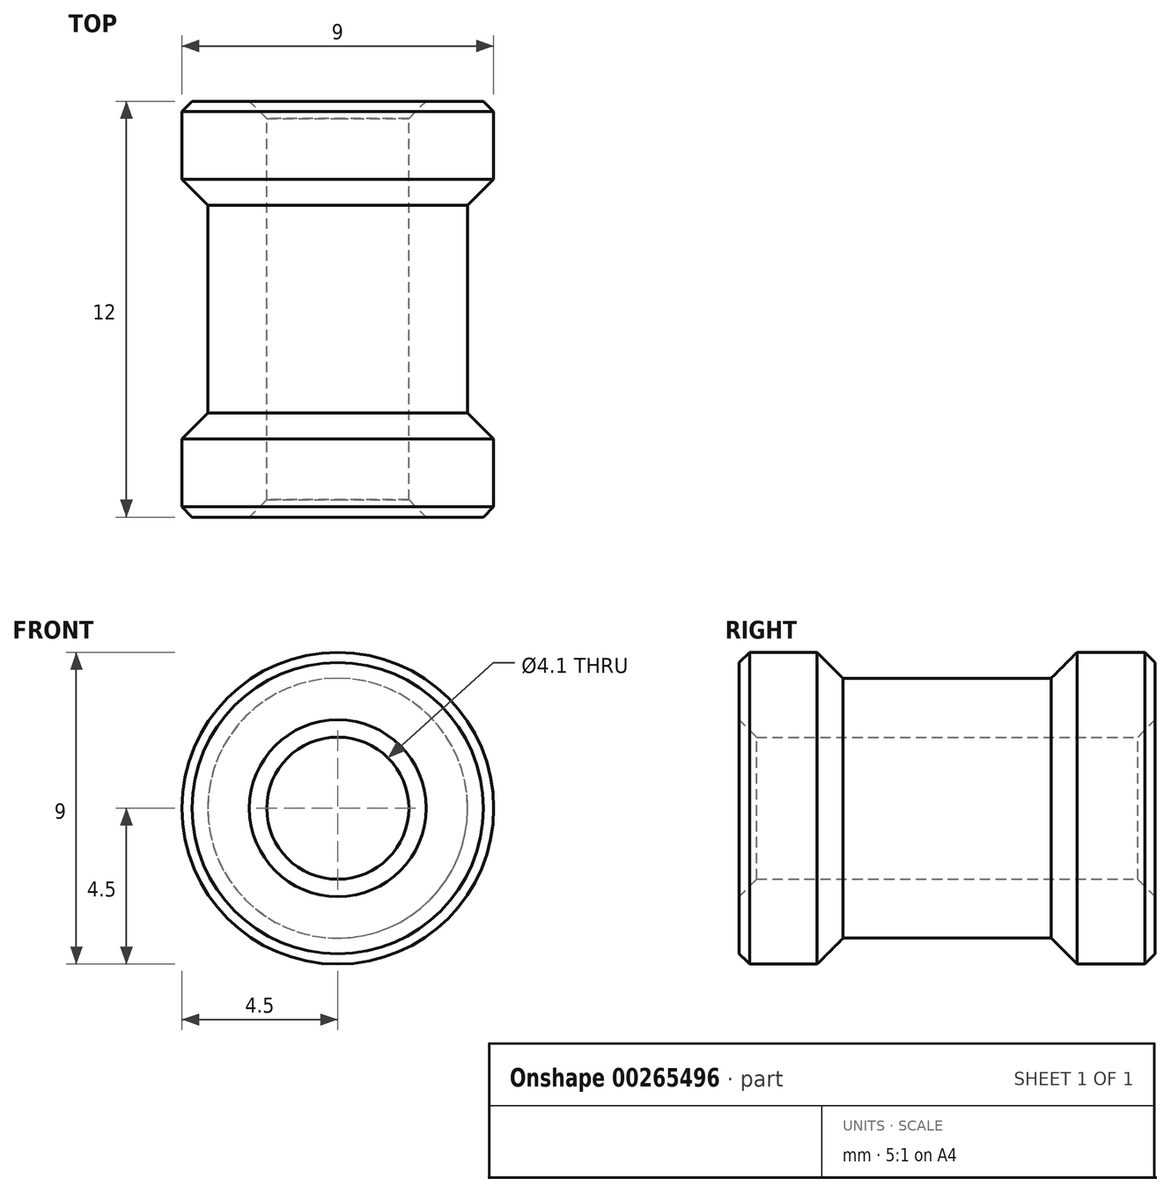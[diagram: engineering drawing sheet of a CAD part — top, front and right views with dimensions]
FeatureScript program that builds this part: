
annotation { "Feature Type Name" : "Feature", "Feature Type Description" : "" }
export const myFeature = defineFeature(function(context is Context, id is Id, definition is map)
    precondition{}
    {
        {
            var Q0;
            Q0=qCreatedBy(makeId("Front.planeOp"),FACE);
            var sketch = newSketch(context, id + "F0", { "sketchPlane" : qUnion([Q0])});
            skCircle(sketch, "E0", {"center": v(0, 0) * mm, "radius": 4.5 * mm});
            skCircle(sketch, "E1", {"center": v(0, 0) * mm, "radius": 2.05 * mm});
            skSolve(sketch);
        }
        {
            var Q0;
            Q0=makeQuery(id+"F0.imprint","IMPRINT",FACE,{"disambiguationData":[TD([[makeQuery(id+"F0.imprint","IMPRINT",EDGE,{"derivedFrom":sQuery(id+"F0.wireOp",EDGE,"E0")}),1.0]])]});
            extrude(context, id + "F1", {"entities" : qUnion([Q0]), "depth" : 12 * mm});
        }
        {
            var Q0;
            Q0=makeQuery(id+"F1.opExtrude","CAP_EDGE",EDGE,{"disambiguationData":[OSD([sQuery(id+"F0.wireOp",EDGE,"E0")])],"isStart":false});
            chamfer(context, id + "F2", {"entities" : qUnion([Q0]), "width" : 0.3 * mm, "tangentPropagation" : true});
        }
        {
            var Q0;
            Q0=makeQuery(id+"F1.opExtrude","CAP_EDGE",EDGE,{"disambiguationData":[OSD([sQuery(id+"F0.wireOp",EDGE,"E1")])],"isStart":false});
            chamfer(context, id + "F3", {"entities" : qUnion([Q0]), "width" : 0.5 * mm, "tangentPropagation" : true});
        }
        {
            var Q0;
            Q0=makeQuery(id+"F1.opExtrude","CAP_EDGE",EDGE,{"disambiguationData":[OSD([sQuery(id+"F0.wireOp",EDGE,"E1")])],"isStart":true});
            chamfer(context, id + "F4", {"entities" : qUnion([Q0]), "width" : 0.5 * mm, "tangentPropagation" : true});
        }
        {
            var Q0;
            Q0=makeQuery(id+"F1.opExtrude","CAP_EDGE",EDGE,{"disambiguationData":[OSD([sQuery(id+"F0.wireOp",EDGE,"E0")])],"isStart":true});
            chamfer(context, id + "F5", {"entities" : qUnion([Q0]), "width" : 0.3 * mm, "tangentPropagation" : true});
        }
        {
            var Q0;
            Q0=qCreatedBy(makeId("Top.planeOp"),FACE);
            var sketch = newSketch(context, id + "F6", { "sketchPlane" : qUnion([Q0])});
            skPoint(sketch, "E2.middle", {"position": v(0, 0) * mm});
            skLineSegment(sketch, "E3", {"start": v(0, 0) * mm, "end": v(0, -2) * mm});
            skLineSegment(sketch, "E4", {"start": v(-3.75, -2) * mm, "end": v(-3.75, -10) * mm});
            skLineSegment(sketch, "E5", {"start": v(-3.75, -10) * mm, "end": v(0, -10) * mm});
            skLineSegment(sketch, "E6", {"start": v(0, -2) * mm, "end": v(-3.75, -2) * mm});
            skLineSegment(sketch, "E7", {"start": v(0, -10) * mm, "end": v(0, -12) * mm});
            skLineSegment(sketch, "E8.bottom", {"start": v(-3.75, -2) * mm, "end": v(-4.53, -2) * mm});
            skLineSegment(sketch, "E8.top", {"start": v(-3.75, -10) * mm, "end": v(-4.53, -10) * mm});
            skLineSegment(sketch, "E8.right", {"start": v(-4.53, -2) * mm, "end": v(-4.53, -10) * mm});
            skLineSegment(sketch, "E9", {"start": v(0, 0) * mm, "end": v(0, 5.28) * mm, "construction": true});
            skSolve(sketch);
        }
        {
            var Q0;
            Q0=makeQuery(id+"F6.imprint","IMPRINT",FACE,{"disambiguationData":[TD([[makeQuery(id+"F6.imprint","IMPRINT",EDGE,{"derivedFrom":sQuery(id+"F6.wireOp",EDGE,"E8.bottom")}),1.0]])]});
            var Q1;
            Q1=sQuery(id+"F6.wireOp",EDGE,"E9");
            revolve(context, id + "F7", {"operationType" : NewBodyOperationType.REMOVE, "entities" : qUnion([Q0]), "axis" : qUnion([Q1]), "revolveType" : RevolveType.FULL, "oppositeDirection" : true});
        }
        {
            var Q0;
            Q0=makeQuery(id+"F7.boolean.opBoolean","COPY",FACE,{"derivedFrom":makeQuery(id+"F7.opRevolve","SWEPT_FACE",FACE,{"disambiguationData":[OSD([sQuery(id+"F6.wireOp",EDGE,"E4")])]})});
            chamfer(context, id + "F8", {"entities" : qUnion([Q0]), "width" : 1 * mm, "tangentPropagation" : true});
        }
    });
